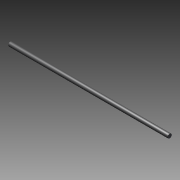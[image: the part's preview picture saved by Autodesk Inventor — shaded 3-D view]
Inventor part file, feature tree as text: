
AUTODESK INVENTOR PART (.ipt)
format: ipt  version: 2011 SP1 (Build 150282100, 282)  size: 74,752 bytes
history: native  units: mm
features: revolve x1, sketch x1
ambient origin geometry x8: Origin, YZ Plane, XZ Plane, XY Plane, X Axis, Y Axis, Z Axis, Center Point
bodies: Solid1 (feature_tree)
feature tree (2):
  revolve  "Revolution1"  [1 undecoded]
  sketch  "Sketch_3"  dims[d0=360.0deg]
note: 1 required parameter value undecoded (feature->parameter linkage not recoverable at this tier; creation-order binding heuristic only, values carry confidence <= 0.55)
